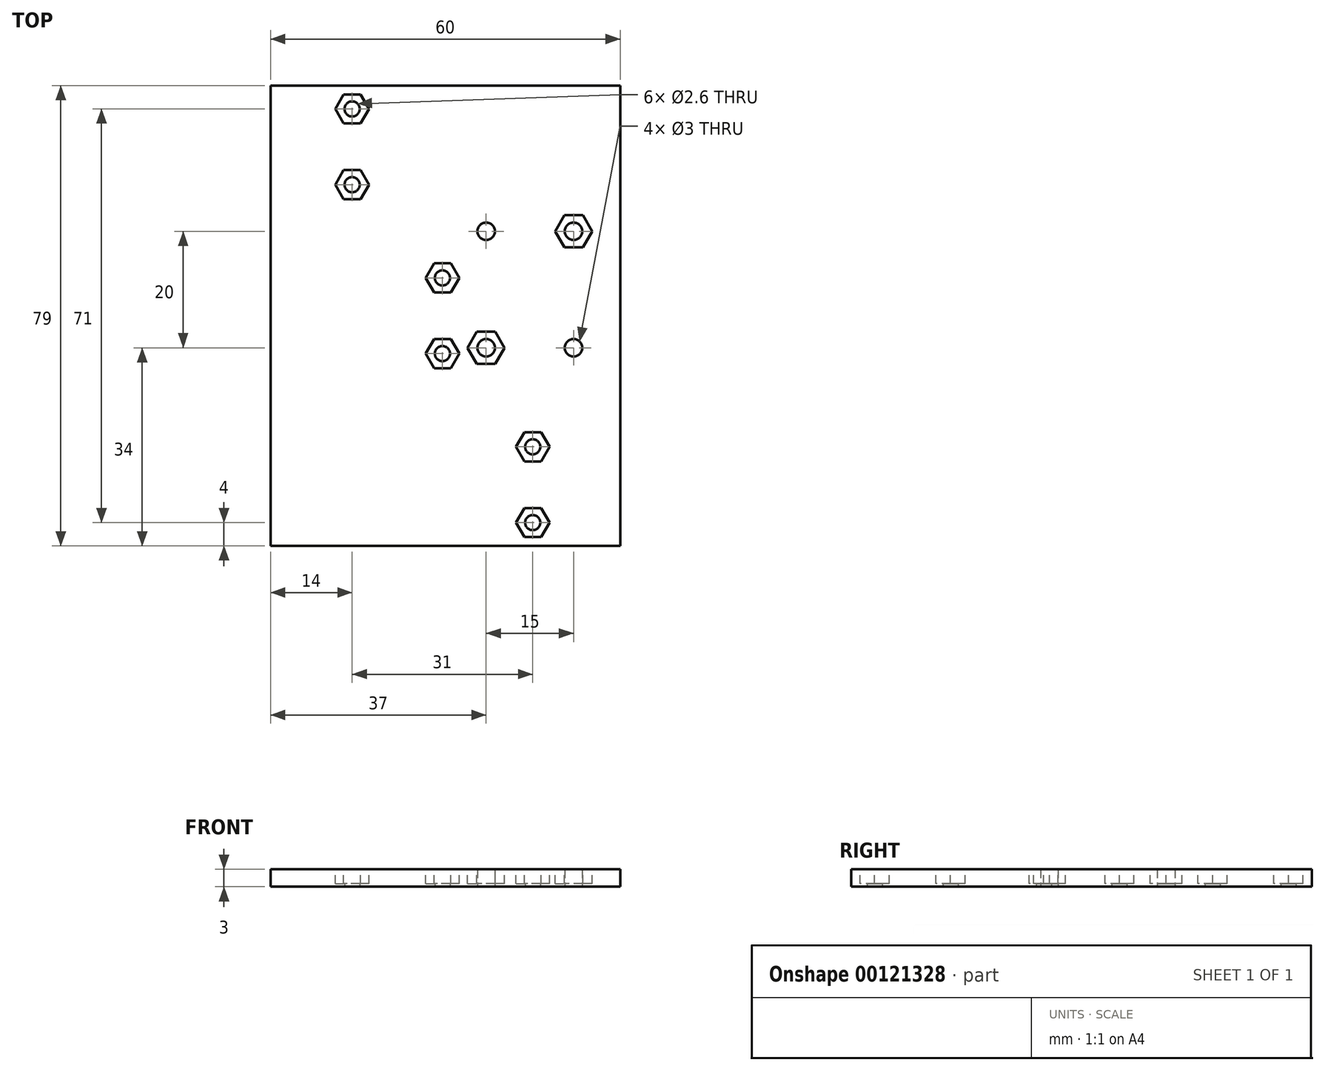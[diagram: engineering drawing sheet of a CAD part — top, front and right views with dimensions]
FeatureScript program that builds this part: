
annotation { "Feature Type Name" : "Feature", "Feature Type Description" : "" }
export const myFeature = defineFeature(function(context is Context, id is Id, definition is map)
    precondition{}
    {
        {
            var Q0;
            Q0=qCreatedBy(makeId("Top.planeOp"),FACE);
            var sketch = newSketch(context, id + "F0", { "sketchPlane" : qUnion([Q0])});
            skLineSegment(sketch, "E0.bottom", {"start": v(1, -20) * mm, "end": v(16.5, -20) * mm, "construction": true});
            skLineSegment(sketch, "E0.top", {"start": v(1, -1) * mm, "end": v(16.5, -1) * mm, "construction": true});
            skLineSegment(sketch, "E0.left", {"start": v(1, -20) * mm, "end": v(1, -1) * mm, "construction": true});
            skLineSegment(sketch, "E0.right", {"start": v(16.5, -20) * mm, "end": v(16.5, -1) * mm, "construction": true});
            skCircle(sketch, "E1", {"center": v(37, -25) * mm, "radius": 1.5 * mm});
            skCircle(sketch, "E2", {"center": v(52, -25) * mm, "radius": 1.5 * mm});
            skCircle(sketch, "E3", {"center": v(37, -45) * mm, "radius": 1.5 * mm});
            skCircle(sketch, "E4", {"center": v(52, -45) * mm, "radius": 1.5 * mm});
            skCircle(sketch, "E5", {"center": v(14, -17) * mm, "radius": 1.3 * mm});
            skCircle(sketch, "E6", {"center": v(14, -4) * mm, "radius": 1.3 * mm});
            skLineSegment(sketch, "E7", {"start": v(14, -4) * mm, "end": v(14, -17) * mm, "construction": true});
            skLineSegment(sketch, "E8.bottom", {"start": v(0, 0) * mm, "end": v(60, 0) * mm});
            skLineSegment(sketch, "E8.left", {"start": v(0, 0) * mm, "end": v(0, -79) * mm});
            skLineSegment(sketch, "E8.right", {"start": v(60, 0) * mm, "end": v(60, -79) * mm});
            skLineSegment(sketch, "E9", {"start": v(16.5, -20) * mm, "end": v(16.5, -30) * mm, "construction": true});
            skLineSegment(sketch, "E10.bottom", {"start": v(16.5, -30) * mm, "end": v(32, -30) * mm, "construction": true});
            skLineSegment(sketch, "E10.top", {"start": v(16.5, -49) * mm, "end": v(32, -49) * mm, "construction": true});
            skLineSegment(sketch, "E10.left", {"start": v(16.5, -30) * mm, "end": v(16.5, -49) * mm, "construction": true});
            skLineSegment(sketch, "E10.right", {"start": v(32, -30) * mm, "end": v(32, -49) * mm, "construction": true});
            skLineSegment(sketch, "E11.bottom", {"start": v(32, -59) * mm, "end": v(47.5, -59) * mm, "construction": true});
            skLineSegment(sketch, "E11.top", {"start": v(32, -78) * mm, "end": v(47.5, -78) * mm, "construction": true});
            skLineSegment(sketch, "E11.left", {"start": v(32, -59) * mm, "end": v(32, -78) * mm, "construction": true});
            skLineSegment(sketch, "E11.right", {"start": v(47.5, -59) * mm, "end": v(47.5, -78) * mm, "construction": true});
            skLineSegment(sketch, "E12", {"start": v(32, -49) * mm, "end": v(32, -59) * mm, "construction": true});
            skLineSegment(sketch, "E13", {"start": v(0, -79) * mm, "end": v(60, -79) * mm});
            skLineSegment(sketch, "E14", {"start": v(1, -20) * mm, "end": v(0, -20) * mm, "construction": true});
            skLineSegment(sketch, "E15", {"start": v(1, -1) * mm, "end": v(1, 0) * mm, "construction": true});
            skLineSegment(sketch, "E16", {"start": v(47.5, -78) * mm, "end": v(47.5, -79) * mm, "construction": true});
            skCircle(sketch, "E17", {"center": v(29.5, -33) * mm, "radius": 1.3 * mm});
            skCircle(sketch, "E18", {"center": v(29.5, -46) * mm, "radius": 1.3 * mm});
            skCircle(sketch, "E19", {"center": v(45, -62) * mm, "radius": 1.3 * mm});
            skCircle(sketch, "E20", {"center": v(45, -75) * mm, "radius": 1.3 * mm});
            skLineSegment(sketch, "E21", {"start": v(29.5, -33) * mm, "end": v(16.5, -33) * mm, "construction": true});
            skLineSegment(sketch, "E22", {"start": v(16.5, -33) * mm, "end": v(29.5, -33) * mm, "construction": true});
            skLineSegment(sketch, "E23", {"start": v(29.5, -46) * mm, "end": v(29.5, -33) * mm, "construction": true});
            skLineSegment(sketch, "E24", {"start": v(45, -62) * mm, "end": v(32, -62) * mm, "construction": true});
            skLineSegment(sketch, "E25", {"start": v(32, -62) * mm, "end": v(45, -62) * mm, "construction": true});
            skLineSegment(sketch, "E26", {"start": v(45, -75) * mm, "end": v(45, -62) * mm, "construction": true});
            skLineSegment(sketch, "E27", {"start": v(14, -4) * mm, "end": v(1, -4) * mm, "construction": true});
            skLineSegment(sketch, "E28", {"start": v(14, -4) * mm, "end": v(14, -1) * mm, "construction": true});
            skLineSegment(sketch, "E29", {"start": v(29.5, -33) * mm, "end": v(29.5, -30) * mm, "construction": true});
            skLineSegment(sketch, "E30", {"start": v(45, -62) * mm, "end": v(45, -59) * mm, "construction": true});
            skLineSegment(sketch, "E31", {"start": v(14, -17) * mm, "end": v(14, -20) * mm, "construction": true});
            skSolve(sketch);
        }
        {
            var Q0;
            Q0=makeQuery(id+"F0.imprint","IMPRINT",FACE,{"disambiguationData":[TD([[makeQuery(id+"F0.imprint","IMPRINT",EDGE,{"derivedFrom":sQuery(id+"F0.wireOp",EDGE,"E1")}),-1.0]])]});
            var Q1;
            Q1=sQuery(id+"F0.wireOp",EDGE,"E0.left");
            var Q2;
            Q2=sQuery(id+"F0.wireOp",EDGE,"E0.bottom");
            var Q3;
            Q3=sQuery(id+"F0.wireOp",EDGE,"E0.right");
            var Q4;
            Q4=sQuery(id+"F0.wireOp",EDGE,"E0.top");
            var Q5;
            Q5=sQuery(id+"F0.wireOp",EDGE,"E10.bottom");
            var Q6;
            Q6=sQuery(id+"F0.wireOp",EDGE,"E10.left");
            var Q7;
            Q7=sQuery(id+"F0.wireOp",EDGE,"E10.top");
            var Q8;
            Q8=sQuery(id+"F0.wireOp",EDGE,"E10.right");
            var Q9;
            Q9=sQuery(id+"F0.wireOp",EDGE,"E11.bottom");
            var Q10;
            Q10=sQuery(id+"F0.wireOp",EDGE,"E11.right");
            var Q11;
            Q11=sQuery(id+"F0.wireOp",EDGE,"E11.left");
            var Q12;
            Q12=sQuery(id+"F0.wireOp",EDGE,"E11.top");
            extrude(context, id + "F1", {"entities" : qUnion([Q0]), "surfaceEntities" : qUnion([Q1, Q2, Q3, Q4, Q5, Q6, Q7, Q8, Q9, Q10, Q11, Q12]), "depth" : 3 * mm});
        }
        {
            var Q0;
            Q0=makeQuery(id+"F1.opExtrude","CAP_FACE",FACE,{"disambiguationData":[OSD([sQuery(id+"F0.wireOp",EDGE,"E1"),sQuery(id+"F0.wireOp",EDGE,"E2"),sQuery(id+"F0.wireOp",EDGE,"E3"),sQuery(id+"F0.wireOp",EDGE,"E4"),sQuery(id+"F0.wireOp",EDGE,"E5"),sQuery(id+"F0.wireOp",EDGE,"E6"),sQuery(id+"F0.wireOp",EDGE,"E8.bottom"),sQuery(id+"F0.wireOp",EDGE,"E8.left"),sQuery(id+"F0.wireOp",EDGE,"E8.right"),sQuery(id+"F0.wireOp",EDGE,"E13"),sQuery(id+"F0.wireOp",EDGE,"E17"),sQuery(id+"F0.wireOp",EDGE,"E18"),sQuery(id+"F0.wireOp",EDGE,"E19"),sQuery(id+"F0.wireOp",EDGE,"E20")])],"isStart":false});
            var sketch = newSketch(context, id + "F2", { "sketchPlane" : qUnion([Q0])});
            skCircle(sketch, "E32.cCircle", {"center": v(14, -4) * mm, "radius": 2.5 * mm, "construction": true});
            skLineSegment(sketch, "E32.0", {"start": v(15.44, -6.5) * mm, "end": v(12.56, -6.5) * mm});
            skLineSegment(sketch, "E32.1", {"start": v(12.56, -6.5) * mm, "end": v(11.11, -4) * mm});
            skLineSegment(sketch, "E32.2", {"start": v(11.11, -4) * mm, "end": v(12.56, -1.5) * mm});
            skLineSegment(sketch, "E32.3", {"start": v(12.56, -1.5) * mm, "end": v(15.44, -1.5) * mm});
            skLineSegment(sketch, "E32.4", {"start": v(15.44, -1.5) * mm, "end": v(16.89, -4) * mm});
            skLineSegment(sketch, "E32.5", {"start": v(16.89, -4) * mm, "end": v(15.44, -6.5) * mm});
            skPoint(sketch, "E32.0.midPoint", {"position": v(14, -6.5) * mm});
            skCircle(sketch, "E33.cCircle", {"center": v(14, -17) * mm, "radius": 2.5 * mm, "construction": true});
            skLineSegment(sketch, "E33.0", {"start": v(15.44, -19.5) * mm, "end": v(12.56, -19.5) * mm});
            skLineSegment(sketch, "E33.1", {"start": v(12.56, -19.5) * mm, "end": v(11.11, -17) * mm});
            skLineSegment(sketch, "E33.2", {"start": v(11.11, -17) * mm, "end": v(12.56, -14.5) * mm});
            skLineSegment(sketch, "E33.3", {"start": v(12.56, -14.5) * mm, "end": v(15.44, -14.5) * mm});
            skLineSegment(sketch, "E33.4", {"start": v(15.44, -14.5) * mm, "end": v(16.89, -17) * mm});
            skLineSegment(sketch, "E33.5", {"start": v(16.89, -17) * mm, "end": v(15.44, -19.5) * mm});
            skPoint(sketch, "E33.0.midPoint", {"position": v(14, -19.5) * mm});
            skCircle(sketch, "E34.cCircle", {"center": v(29.5, -33) * mm, "radius": 2.5 * mm, "construction": true});
            skLineSegment(sketch, "E34.0", {"start": v(30.94, -35.5) * mm, "end": v(28.06, -35.5) * mm});
            skLineSegment(sketch, "E34.1", {"start": v(28.06, -35.5) * mm, "end": v(26.61, -33) * mm});
            skLineSegment(sketch, "E34.2", {"start": v(26.61, -33) * mm, "end": v(28.06, -30.5) * mm});
            skLineSegment(sketch, "E34.3", {"start": v(28.06, -30.5) * mm, "end": v(30.94, -30.5) * mm});
            skLineSegment(sketch, "E34.4", {"start": v(30.94, -30.5) * mm, "end": v(32.39, -33) * mm});
            skLineSegment(sketch, "E34.5", {"start": v(32.39, -33) * mm, "end": v(30.94, -35.5) * mm});
            skPoint(sketch, "E34.0.midPoint", {"position": v(29.5, -35.5) * mm});
            skCircle(sketch, "E35.cCircle", {"center": v(29.5, -46) * mm, "radius": 2.5 * mm, "construction": true});
            skLineSegment(sketch, "E35.0", {"start": v(30.94, -48.5) * mm, "end": v(28.06, -48.5) * mm});
            skLineSegment(sketch, "E35.1", {"start": v(28.06, -48.5) * mm, "end": v(26.61, -46) * mm});
            skLineSegment(sketch, "E35.2", {"start": v(26.61, -46) * mm, "end": v(28.06, -43.5) * mm});
            skLineSegment(sketch, "E35.3", {"start": v(28.06, -43.5) * mm, "end": v(30.94, -43.5) * mm});
            skLineSegment(sketch, "E35.4", {"start": v(30.94, -43.5) * mm, "end": v(32.39, -46) * mm});
            skLineSegment(sketch, "E35.5", {"start": v(32.39, -46) * mm, "end": v(30.94, -48.5) * mm});
            skPoint(sketch, "E35.0.midPoint", {"position": v(29.5, -48.5) * mm});
            skCircle(sketch, "E36.cCircle", {"center": v(45, -62) * mm, "radius": 2.5 * mm, "construction": true});
            skLineSegment(sketch, "E36.0", {"start": v(46.44, -64.5) * mm, "end": v(43.56, -64.5) * mm});
            skLineSegment(sketch, "E36.1", {"start": v(43.56, -64.5) * mm, "end": v(42.11, -62) * mm});
            skLineSegment(sketch, "E36.2", {"start": v(42.11, -62) * mm, "end": v(43.56, -59.5) * mm});
            skLineSegment(sketch, "E36.3", {"start": v(43.56, -59.5) * mm, "end": v(46.44, -59.5) * mm});
            skLineSegment(sketch, "E36.4", {"start": v(46.44, -59.5) * mm, "end": v(47.89, -62) * mm});
            skLineSegment(sketch, "E36.5", {"start": v(47.89, -62) * mm, "end": v(46.44, -64.5) * mm});
            skPoint(sketch, "E36.0.midPoint", {"position": v(45, -64.5) * mm});
            skCircle(sketch, "E37.cCircle", {"center": v(45, -75) * mm, "radius": 2.5 * mm, "construction": true});
            skLineSegment(sketch, "E37.0", {"start": v(46.44, -77.5) * mm, "end": v(43.56, -77.5) * mm});
            skLineSegment(sketch, "E37.1", {"start": v(43.56, -77.5) * mm, "end": v(42.11, -75) * mm});
            skLineSegment(sketch, "E37.2", {"start": v(42.11, -75) * mm, "end": v(43.56, -72.5) * mm});
            skLineSegment(sketch, "E37.3", {"start": v(43.56, -72.5) * mm, "end": v(46.44, -72.5) * mm});
            skLineSegment(sketch, "E37.4", {"start": v(46.44, -72.5) * mm, "end": v(47.89, -75) * mm});
            skLineSegment(sketch, "E37.5", {"start": v(47.89, -75) * mm, "end": v(46.44, -77.5) * mm});
            skPoint(sketch, "E37.0.midPoint", {"position": v(45, -77.5) * mm});
            skCircle(sketch, "E38.cCircle", {"center": v(52, -25) * mm, "radius": 2.75 * mm, "construction": true});
            skLineSegment(sketch, "E38.0", {"start": v(53.59, -27.75) * mm, "end": v(50.41, -27.75) * mm});
            skLineSegment(sketch, "E38.1", {"start": v(50.41, -27.75) * mm, "end": v(48.82, -25) * mm});
            skLineSegment(sketch, "E38.2", {"start": v(48.82, -25) * mm, "end": v(50.41, -22.25) * mm});
            skLineSegment(sketch, "E38.3", {"start": v(50.41, -22.25) * mm, "end": v(53.59, -22.25) * mm});
            skLineSegment(sketch, "E38.4", {"start": v(53.59, -22.25) * mm, "end": v(55.18, -25) * mm});
            skLineSegment(sketch, "E38.5", {"start": v(55.18, -25) * mm, "end": v(53.59, -27.75) * mm});
            skPoint(sketch, "E38.0.midPoint", {"position": v(52, -27.75) * mm});
            skCircle(sketch, "E39.cCircle", {"center": v(37, -45) * mm, "radius": 2.75 * mm, "construction": true});
            skLineSegment(sketch, "E39.0", {"start": v(38.59, -47.75) * mm, "end": v(35.41, -47.75) * mm});
            skLineSegment(sketch, "E39.1", {"start": v(35.41, -47.75) * mm, "end": v(33.82, -45) * mm});
            skLineSegment(sketch, "E39.2", {"start": v(33.82, -45) * mm, "end": v(35.41, -42.25) * mm});
            skLineSegment(sketch, "E39.3", {"start": v(35.41, -42.25) * mm, "end": v(38.59, -42.25) * mm});
            skLineSegment(sketch, "E39.4", {"start": v(38.59, -42.25) * mm, "end": v(40.18, -45) * mm});
            skLineSegment(sketch, "E39.5", {"start": v(40.18, -45) * mm, "end": v(38.59, -47.75) * mm});
            skPoint(sketch, "E39.0.midPoint", {"position": v(37, -47.75) * mm});
            skSolve(sketch);
        }
        {
            var Q0;
            Q0 = qSketchRegion(id + "F2", true);
            extrude(context, id + "F3", {"entities" : qUnion([Q0]), "operationType" : NewBodyOperationType.REMOVE, "oppositeDirection" : true, "depth" : 2.5 * mm});
        }
    });
